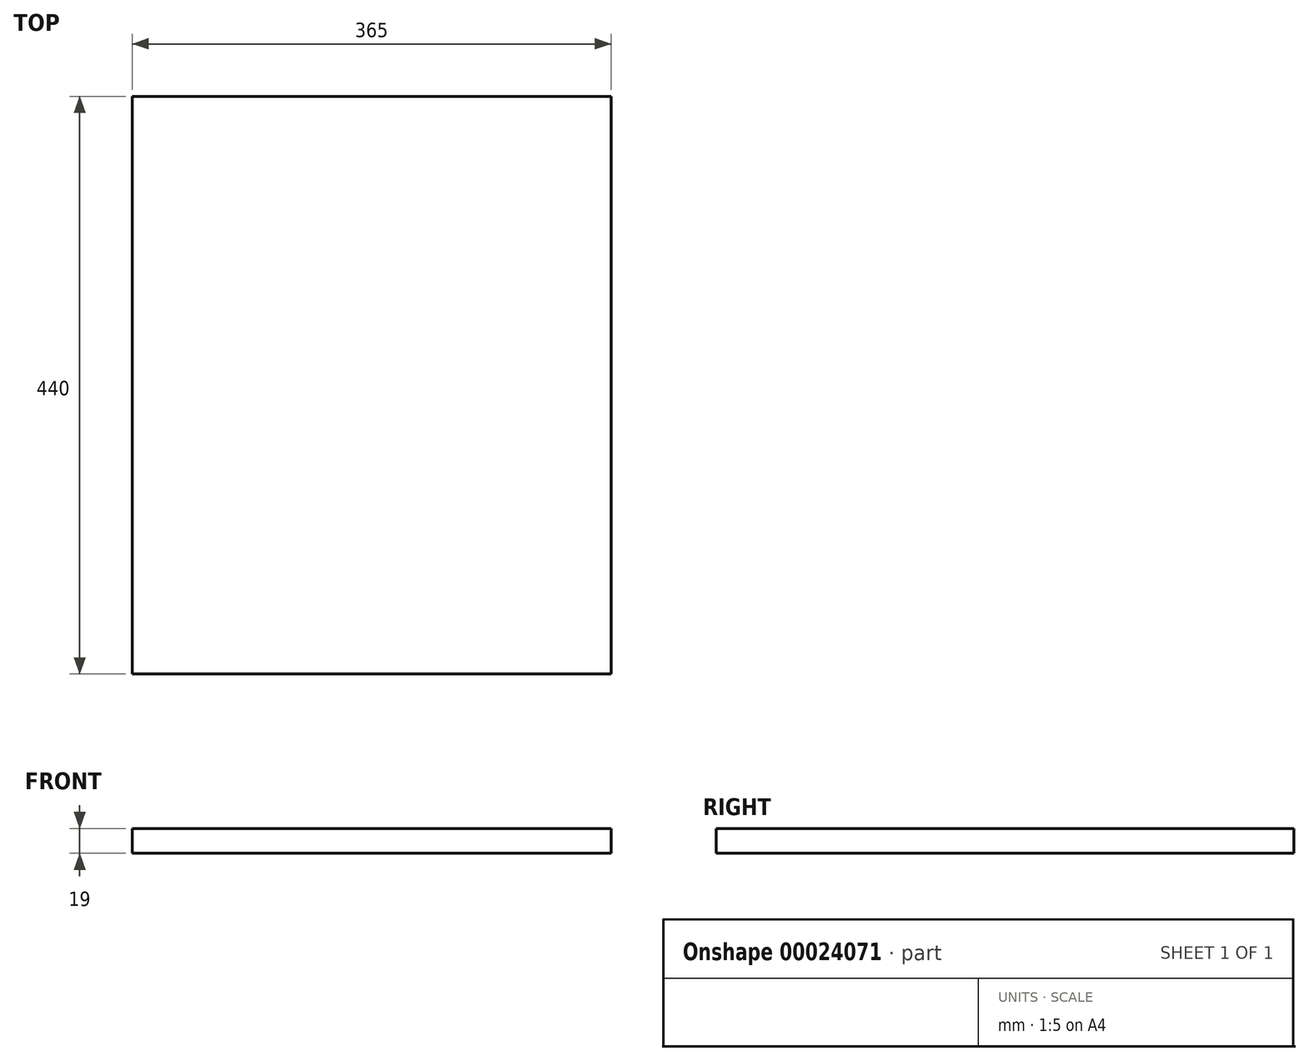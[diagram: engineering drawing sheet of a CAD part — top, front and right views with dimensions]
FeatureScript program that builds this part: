
annotation { "Feature Type Name" : "Feature", "Feature Type Description" : "" }
export const myFeature = defineFeature(function(context is Context, id is Id, definition is map)
    precondition{}
    {
        {
            var Q0;
            Q0=qCreatedBy(makeId("Top.planeOp"),FACE);
            var sketch = newSketch(context, id + "F0", { "sketchPlane" : qUnion([Q0])});
            skLineSegment(sketch, "E0.bottom", {"start": v(-70.96, 65.05) * mm, "end": v(294.04, 65.05) * mm});
            skLineSegment(sketch, "E0.top", {"start": v(-70.96, -374.95) * mm, "end": v(294.04, -374.95) * mm});
            skLineSegment(sketch, "E0.left", {"start": v(-70.96, 65.05) * mm, "end": v(-70.96, -374.95) * mm});
            skLineSegment(sketch, "E0.right", {"start": v(294.04, 65.05) * mm, "end": v(294.04, -374.95) * mm});
            skSolve(sketch);
        }
        {
            var Q0;
            Q0=qSketchRegion(id+"F0",true);
            extrude(context, id + "F1", {"entities" : qUnion([Q0]), "depth" : 19 * mm});
        }
    });
